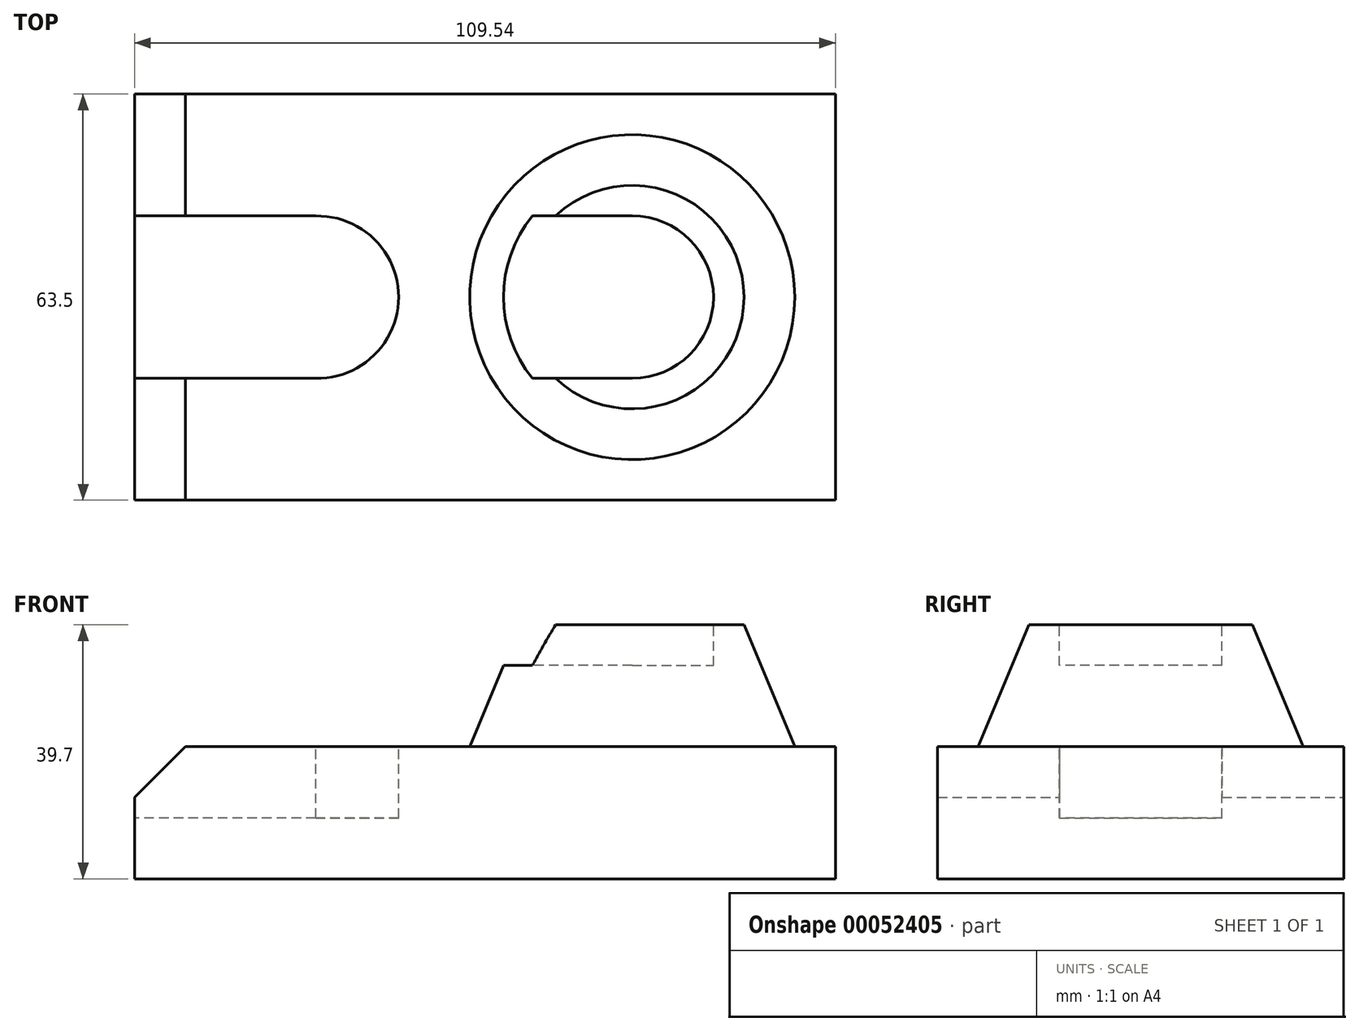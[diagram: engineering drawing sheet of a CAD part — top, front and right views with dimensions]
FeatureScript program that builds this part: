
annotation { "Feature Type Name" : "Feature", "Feature Type Description" : "" }
export const myFeature = defineFeature(function(context is Context, id is Id, definition is map)
    precondition{}
    {
        {
            var Q0;
            Q0=qCreatedBy(makeId("Top.planeOp"),FACE);
            var sketch = newSketch(context, id + "F0", { "sketchPlane" : qUnion([Q0])});
            skLineSegment(sketch, "E0.bottom", {"start": v(-77.79, 31.75) * mm, "end": v(31.75, 31.75) * mm});
            skLineSegment(sketch, "E0.top", {"start": v(-77.79, -31.75) * mm, "end": v(31.75, -31.75) * mm});
            skLineSegment(sketch, "E0.left", {"start": v(-77.79, 31.75) * mm, "end": v(-77.79, -31.75) * mm});
            skLineSegment(sketch, "E0.right", {"start": v(31.75, 31.75) * mm, "end": v(31.75, -31.75) * mm});
            skSolve(sketch);
        }
        {
            var Q0;
            Q0=makeQuery(id+"F0.imprint","IMPRINT",FACE,{"disambiguationData":[TD([[makeQuery(id+"F0.imprint","IMPRINT",EDGE,{"derivedFrom":sQuery(id+"F0.wireOp",EDGE,"E0.bottom")}),-1.0]])]});
            extrude(context, id + "F1", {"entities" : qUnion([Q0]), "depth" : 20.65 * mm});
        }
        {
            var Q0;
            Q0=qCreatedBy(makeId("Right.planeOp"),FACE);
            var sketch = newSketch(context, id + "F2", { "sketchPlane" : qUnion([Q0])});
            skLineSegment(sketch, "E1", {"start": v(25.4, 20.65) * mm, "end": v(17.46, 39.7) * mm});
            skLineSegment(sketch, "E2", {"start": v(17.46, 39.7) * mm, "end": v(0, 39.7) * mm});
            skLineSegment(sketch, "E3", {"start": v(0, 39.7) * mm, "end": v(0, 20.65) * mm});
            skLineSegment(sketch, "E4.0", {"start": v(25.4, 20.65) * mm, "end": v(0, 20.65) * mm});
            skPoint(sketch, "E5.orphan", {"position": v(-31.75, 20.65) * mm});
            skPoint(sketch, "E6.orphan", {"position": v(31.75, 20.65) * mm});
            skSolve(sketch);
        }
        {
            var Q0;
            Q0 = qSketchRegion(id + "F2", true);
            var Q1;
            Q1=sQuery(id+"F2.wireOp",EDGE,"E3");
            revolve(context, id + "F3", {"operationType" : NewBodyOperationType.ADD, "entities" : qUnion([Q0]), "axis" : qUnion([Q1]), "revolveType" : RevolveType.FULL});
        }
        {
            var Q0;
            Q0=makeQuery(id+"F3.opRevolve","SWEPT_FACE",FACE,{"disambiguationData":[OSD([sQuery(id+"F2.wireOp",EDGE,"E2")])]});
            var sketch = newSketch(context, id + "F4", { "sketchPlane" : qUnion([Q0])});
            skArc(sketch, "E7", {"start": v(0, -12.7) * mm, "mid": v(12.7, 0) * mm, "end": v(0, 12.7) * mm});
            skLineSegment(sketch, "E8", {"start": v(0, -12.7) * mm, "end": v(-30.74, -12.7) * mm});
            skLineSegment(sketch, "E9", {"start": v(-30.74, -12.7) * mm, "end": v(-30.74, 12.7) * mm});
            skLineSegment(sketch, "E10", {"start": v(0, 12.7) * mm, "end": v(-30.74, 12.7) * mm});
            skSolve(sketch);
        }
        {
            var Q0;
            {var subQ0=sQuery(id+"F4.wireOp",EDGE,"E9");Q0=makeQuery(id+"F4.imprint","IMPRINT",FACE,{"disambiguationData":[TD([[makeQuery(id+"F4.imprint","IMPRINT",EDGE,{"derivedFrom":subQ0}),-1.0]])]});}
            var Q1;
            {var subQ0=sQuery(id+"F4.wireOp",EDGE,"E7");Q1=makeQuery(id+"F4.imprint","IMPRINT",FACE,{"disambiguationData":[TD([[makeQuery(id+"F4.imprint","IMPRINT",EDGE,{"derivedFrom":subQ0}),1.0]])]});}
            extrude(context, id + "F5", {"entities" : qUnion([Q0, Q1]), "operationType" : NewBodyOperationType.REMOVE, "oppositeDirection" : true, "depth" : 6.35 * mm});
        }
        {
            var Q0;
            Q0=makeQuery(id+"F1.opExtrude","CAP_FACE",FACE,{"disambiguationData":[OSD([sQuery(id+"F0.wireOp",EDGE,"E0.bottom"),sQuery(id+"F0.wireOp",EDGE,"E0.top"),sQuery(id+"F0.wireOp",EDGE,"E0.left"),sQuery(id+"F0.wireOp",EDGE,"E0.right")])],"isStart":false});
            var sketch = newSketch(context, id + "F6", { "sketchPlane" : qUnion([Q0])});
            skArc(sketch, "E11", {"start": v(-49.46, -12.7) * mm, "mid": v(-36.51, 0) * mm, "end": v(-49.45, 12.7) * mm});
            skLineSegment(sketch, "E12.0", {"start": v(-77.79, 31.75) * mm, "end": v(-77.79, -31.75) * mm});
            skLineSegment(sketch, "E13", {"start": v(-49.45, 12.7) * mm, "end": v(-77.79, 12.7) * mm});
            skLineSegment(sketch, "E14", {"start": v(-49.46, -12.7) * mm, "end": v(-77.79, -12.7) * mm});
            skSolve(sketch);
        }
        {
            var Q0;
            Q0 = qSketchRegion(id + "F6", true);
            extrude(context, id + "F7", {"entities" : qUnion([Q0]), "operationType" : NewBodyOperationType.REMOVE, "oppositeDirection" : true, "depth" : 11.13 * mm});
        }
        {
            var Q0;
            {var subQ0=sQuery(id+"F0.wireOp",EDGE,"E0.bottom");var subQ1=sQuery(id+"F0.wireOp",EDGE,"E0.left");Q0=makeQuery(id+"F7.boolean.opBoolean","SPLIT",EDGE,{"disambiguationData":[TD([makeQuery(id+"F1.opExtrude","SWEPT_FACE",FACE,{"disambiguationData":[OSD([subQ0])]})])],"derivedFrom":makeQuery(id+"F1.opExtrude","CAP_EDGE",EDGE,{"disambiguationData":[OSD([subQ1])],"isStart":false})});}
            var Q1;
            {var subQ0=sQuery(id+"F0.wireOp",EDGE,"E0.left");var subQ1=sQuery(id+"F0.wireOp",EDGE,"E0.top");Q1=makeQuery(id+"F7.boolean.opBoolean","SPLIT",EDGE,{"disambiguationData":[TD([makeQuery(id+"F1.opExtrude","SWEPT_FACE",FACE,{"disambiguationData":[OSD([subQ1])]})])],"derivedFrom":makeQuery(id+"F1.opExtrude","CAP_EDGE",EDGE,{"disambiguationData":[OSD([subQ0])],"isStart":false})});}
            chamfer(context, id + "F8", {"entities" : qUnion([Q0, Q1]), "width" : 7.94 * mm, "tangentPropagation" : true});
        }
    });
